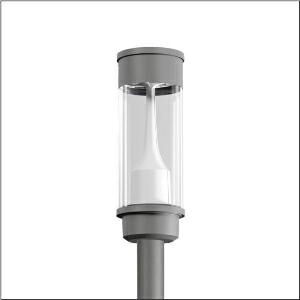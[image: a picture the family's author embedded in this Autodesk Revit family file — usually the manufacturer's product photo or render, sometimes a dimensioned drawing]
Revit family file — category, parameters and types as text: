
# Revit family: litepole_iq___st1_2a_5xa5415ef14h_6754
name_source: partatom
category: Lighting Fixtures
units: mm (PartAtom-declared; Revit-internal decimal feet)

## family parameters
Cut with Voids When Loaded = No
Host = Face
Light Source = No
Part Type = Normal
Room Calculation Point = No
Round Connector Dimension = Use Diameter
Shared = No

## types (1)
- --- (1 x LED, 1540 lm, 10.5 W, 3000K)
    Apparent Load = 11 VA
    CIE Flux Codes = 22 61 93 96 100
    Color Rendering = 70
    Color Temperature = 3000K
    Default Elevation = 1800 mm
    Description = Litepole iQ, mast luminaire, Module 540 iQ-SR, primary light control with 3 zone facetted reflector, of plastic, silver coated, highly specular, structured, primary optical cover: cover, of PMMA, transparent, light distribution: ST1.2a, light emission: direct distribution, primary light characteristic: asymmetric, installation type: post-top, LED, High Power LED, rated luminous flux: 1.540lm, luminous efficacy: 147lm/W, light colour: 730, colour temperature: 3000K, control gear: ECG iQ, control: Auto-Match, Temp-Guard, Lumen-Switch, Night-Set, Smart-Wire, Light-Fading, Desk-Remote (wireless, voltage-free reading and setting of iQ features in the workshop via application-optimized NFC function/RFID function), optimised constant luminous flux control (CLO 2.0), Street-Remote, presetting dimming logarithmic, with terminal, 6-pole, max. 2.5mm², mains connection: 230..240V, AC, 50/60Hz, start of lifetime: 11W, end of service life: 11W, reduction: 5W, luminaire housing, upper part, of glass-fibre reinforced polyester, coated, Siteco® metallic grey (DB 702S), diameter: 210mm, height: 590mm, spigot size: d x l = 76 x 70mm (post-top) | with reducer (optional accessory) 60 x 70mm, post-top mast mounting element, of diecast aluminium, coated, Siteco® metallic grey (DB 702S), Module 540 iQ-SR, traffic white (RAL 9016), equipment: standard, protection rating (complete): IP65, insulation class (complete): insulation class II (safety insulation), certification: CE, ENEC, VDE, packaging unit: 1 piece

Light Distribution: ST1.2a
    Height = 590 mm
    Lamp = 1 x LED
    Lamp Light Flux = 1540 lm
    Lamp Power = 10.5 W
    Lamp count = 1
    Length = 220 mm
    Luminous efficacy = 147 lm/W
    Manufacturer = Siteco
    ModVariant = No
    Model = 5XA5415EF14H
    Number of Poles = 1
    OnlyDefault = Yes
    Power Factor = 1
    Product Name = Litepole iQ | ST1.2a
    Product group = mast luminaire | pylon top
    ProductGroupID = 6100
    Protection Class = Protection class II
    Protection Degree = IP 65
    RLX_Detail_Level = 1
    RLX_Emergency_Light_Flux = 0 lm
    RLX_Emergency_Type = 0
    RLX_Emergency_Type_DB = No
    RlxData = <blob elided: 72169 chars, md5=ae944392>
    Socket = socket
    Standby Power = 0 W
    System Light Flux = 1540 lm
    System Power = 11 W
    Type Comments = factory setting: luminous flux: 100 % | dim-lin: 254 | 419 mA
    Type Image = l_1006025.jpg
    URL = http://relux.com
    VarID = @adj_091183
    Voltage = 0 V
    Weight = 0.00 kg
    Width = 0 mm  [stored 0 ft]

note: [stored X ft] marks values corroborated as IEEE doubles in the binary element streams (Revit-internal decimal feet)

## geometry (parser evidence)
native form markers: Blend x4, Sweep x11
no freeform markers — native parametric forms only
